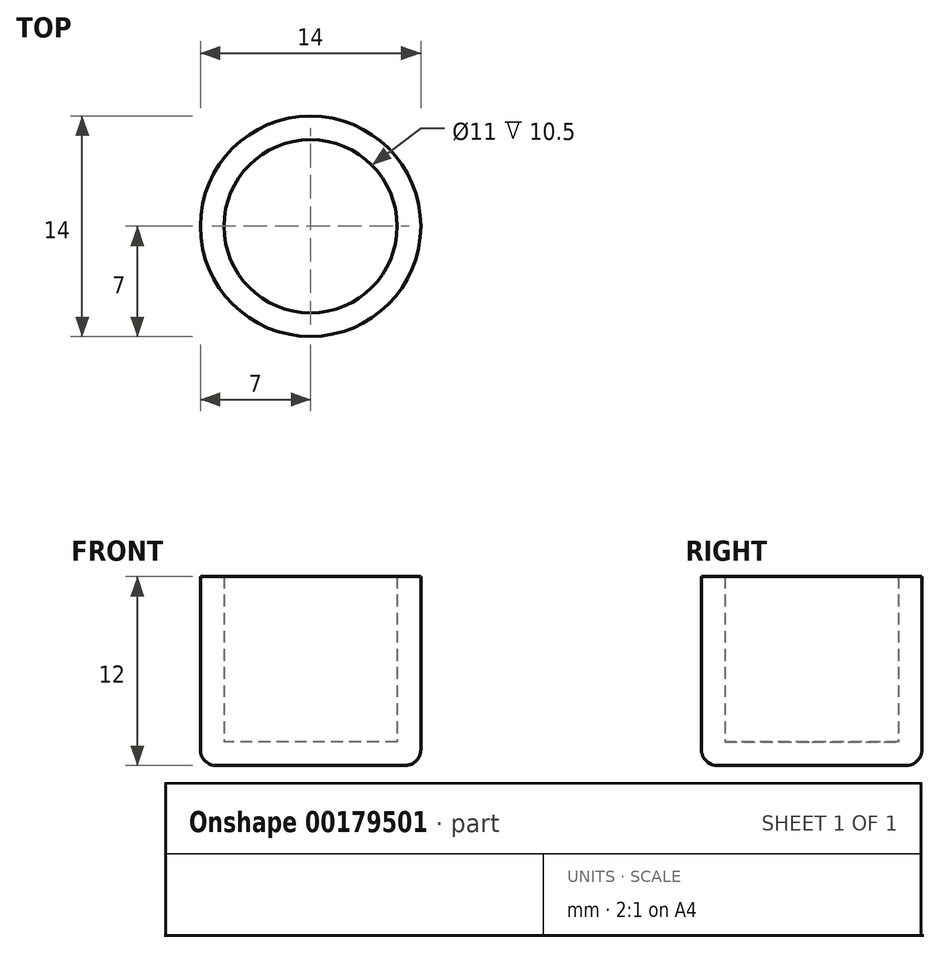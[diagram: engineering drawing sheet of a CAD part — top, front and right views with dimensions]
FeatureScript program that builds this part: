
annotation { "Feature Type Name" : "Feature", "Feature Type Description" : "" }
export const myFeature = defineFeature(function(context is Context, id is Id, definition is map)
    precondition{}
    {
        {
            var Q0;
            Q0=qCreatedBy(makeId("Top.planeOp"),FACE);
            var sketch = newSketch(context, id + "F0", { "sketchPlane" : qUnion([Q0])});
            skCircle(sketch, "E0", {"center": v(0, 0) * mm, "radius": 7 * mm});
            skSolve(sketch);
        }
        {
            var Q0;
            Q0 = qSketchRegion(id + "F0", true);
            extrude(context, id + "F1", {"entities" : qUnion([Q0]), "depth" : 12 * mm});
        }
        {
            var Q0;
            Q0=makeQuery(id+"F1.opExtrude","CAP_FACE",FACE,{"disambiguationData":[OSD([sQuery(id+"F0.wireOp",EDGE,"E0")])],"isStart":false});
            shell(context, id + "F2", {"entities" : qUnion([Q0]), "thickness" : 1.5 * mm});
        }
        {
            var Q0;
            Q0=makeQuery(id+"F1.opExtrude","CAP_EDGE",EDGE,{"disambiguationData":[OSD([sQuery(id+"F0.wireOp",EDGE,"E0")])],"isStart":true});
            fillet(context, id + "F3", {"entities" : qUnion([Q0]), "radius" : 1 * mm, "tangentPropagation" : true, "allowEdgeOverflow" : false});
        }
    });
